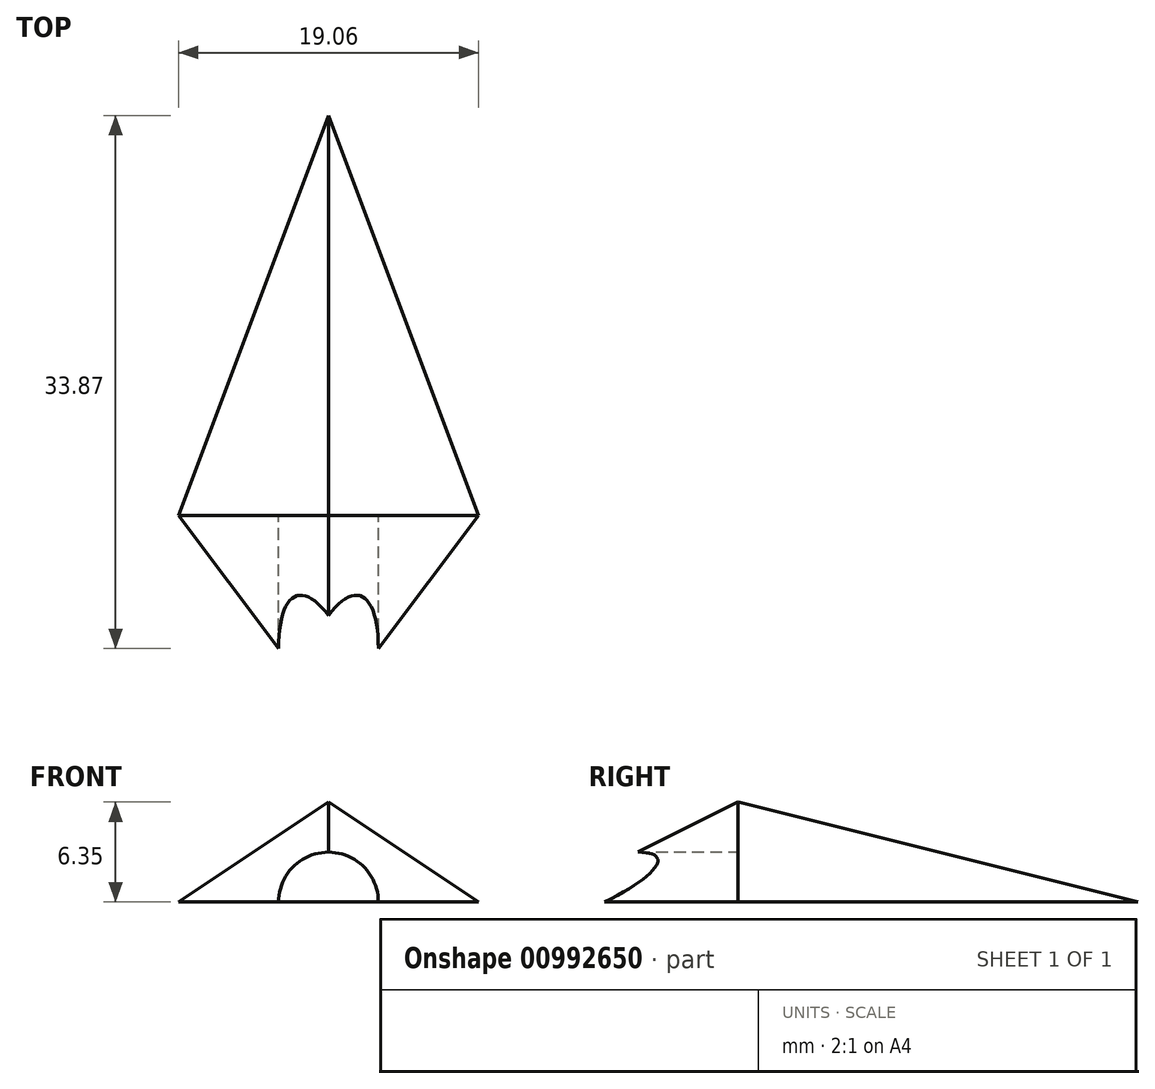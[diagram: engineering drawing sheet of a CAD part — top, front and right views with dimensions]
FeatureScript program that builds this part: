
annotation { "Feature Type Name" : "Feature", "Feature Type Description" : "" }
export const myFeature = defineFeature(function(context is Context, id is Id, definition is map)
    precondition{}
    {
        {
            var Q0;
            Q0=qCreatedBy(makeId("Top.planeOp"),FACE);
            var sketch = newSketch(context, id + "F0", { "sketchPlane" : qUnion([Q0])});
            skLineSegment(sketch, "E0", {"start": v(-9.53, 0) * mm, "end": v(9.53, 0) * mm});
            skLineSegment(sketch, "E1", {"start": v(0, -12.7) * mm, "end": v(0, 25.4) * mm});
            skLineSegment(sketch, "E2", {"start": v(-9.52, 0) * mm, "end": v(0, 25.4) * mm});
            skLineSegment(sketch, "E3", {"start": v(9.52, 0) * mm, "end": v(0, 25.4) * mm});
            skLineSegment(sketch, "E4", {"start": v(-9.53, 0) * mm, "end": v(0, -12.7) * mm});
            skLineSegment(sketch, "E5", {"start": v(9.53, 0) * mm, "end": v(0, -12.7) * mm});
            skSolve(sketch);
        }
        {
            var Q0;
            Q0=qCreatedBy(makeId("Right.planeOp"),FACE);
            var sketch = newSketch(context, id + "F1", { "sketchPlane" : qUnion([Q0])});
            skLineSegment(sketch, "E6", {"start": v(-12.7, 0) * mm, "end": v(25.4, 0) * mm});
            skLineSegment(sketch, "E7", {"start": v(0, 0) * mm, "end": v(0, 6.35) * mm});
            skLineSegment(sketch, "E8", {"start": v(25.4, 0) * mm, "end": v(0, 6.35) * mm});
            skLineSegment(sketch, "E9", {"start": v(-12.7, 0) * mm, "end": v(0, 6.35) * mm});
            skSolve(sketch);
        }
        {
            var Q0;
            Q0=qCreatedBy(makeId("Front.planeOp"),FACE);
            var sketch = newSketch(context, id + "F2", { "sketchPlane" : qUnion([Q0])});
            skLineSegment(sketch, "E10", {"start": v(-9.53, 0) * mm, "end": v(0, 6.35) * mm});
            skLineSegment(sketch, "E11", {"start": v(0, 6.35) * mm, "end": v(9.53, 0) * mm});
            skLineSegment(sketch, "E12", {"start": v(9.53, 0) * mm, "end": v(-9.53, 0) * mm});
            skSolve(sketch);
        }
        {
            var Q0;
            {var subQ2=sQuery(id+"F1.wireOp",EDGE,"E7");Q0=makeQuery(id+"F1.imprint","IMPRINT",FACE,{"disambiguationData":[TD([[makeQuery(id+"F1.imprint","IMPRINT",EDGE,{"derivedFrom":subQ2}),-1.0]])]});}
            var Q1;
            {var subQ0=sQuery(id+"F0.wireOp",EDGE,"E2");Q1=makeQuery(id+"F0.imprint","IMPRINT",FACE,{"disambiguationData":[TD([[makeQuery(id+"F0.imprint","IMPRINT",EDGE,{"derivedFrom":subQ0}),-1.0]])]});}
            var Q2;
            Q2=sQuery(id+"F2.wireOp",EDGE,"E10");
            loft(context, id + "F3", {"addGuides" : true, "sheetProfilesArray" : [{ "sheetProfileEntities" : qUnion([Q0]) }, { "sheetProfileEntities" : qUnion([Q1]) }], "guidesArray" : [{ "guideEntities" : qUnion([Q2]), "guideDerivativeType" : LoftGuideDerivativeType.DEFAULT, "guideDerivativeMagnitude" : 1 }]});
        }
        {
            var Q1;
            {var subQ2=sQuery(id+"F1.wireOp",EDGE,"E7");Q1=makeQuery(id+"F1.imprint","IMPRINT",FACE,{"disambiguationData":[TD([[makeQuery(id+"F1.imprint","IMPRINT",EDGE,{"derivedFrom":subQ2}),1.0]])]});}
            var Q2;
            {var subQ0=sQuery(id+"F0.wireOp",EDGE,"E4");Q2=makeQuery(id+"F0.imprint","IMPRINT",FACE,{"disambiguationData":[TD([[makeQuery(id+"F0.imprint","IMPRINT",EDGE,{"derivedFrom":subQ0}),1.0]])]});}
            var Q3;
            Q3=sQuery(id+"F2.wireOp",EDGE,"E10");
            loft(context, id + "F4", {"operationType" : NewBodyOperationType.ADD, "addGuides" : true, "sheetProfilesArray" : [{ "sheetProfileEntities" : qUnion([Q1]) }, { "sheetProfileEntities" : qUnion([Q2]) }], "guidesArray" : [{ "guideEntities" : qUnion([Q3]), "guideDerivativeType" : LoftGuideDerivativeType.DEFAULT, "guideDerivativeMagnitude" : 1 }]});
        }
        {
            var Q1;
            {var subQ2=sQuery(id+"F1.wireOp",EDGE,"E7");Q1=makeQuery(id+"F1.imprint","IMPRINT",FACE,{"disambiguationData":[TD([[makeQuery(id+"F1.imprint","IMPRINT",EDGE,{"derivedFrom":subQ2}),1.0]])]});}
            var Q2;
            {var subQ0=sQuery(id+"F0.wireOp",EDGE,"E5");Q2=makeQuery(id+"F0.imprint","IMPRINT",FACE,{"disambiguationData":[TD([[makeQuery(id+"F0.imprint","IMPRINT",EDGE,{"derivedFrom":subQ0}),-1.0]])]});}
            var Q3;
            Q3=sQuery(id+"F2.wireOp",EDGE,"E11");
            loft(context, id + "F5", {"operationType" : NewBodyOperationType.ADD, "addGuides" : true, "sheetProfilesArray" : [{ "sheetProfileEntities" : qUnion([Q1]) }, { "sheetProfileEntities" : qUnion([Q2]) }], "guidesArray" : [{ "guideEntities" : qUnion([Q3]), "guideDerivativeType" : LoftGuideDerivativeType.DEFAULT, "guideDerivativeMagnitude" : 1 }]});
        }
        {
            var Q1;
            {var subQ2=sQuery(id+"F1.wireOp",EDGE,"E7");Q1=makeQuery(id+"F1.imprint","IMPRINT",FACE,{"disambiguationData":[TD([[makeQuery(id+"F1.imprint","IMPRINT",EDGE,{"derivedFrom":subQ2}),-1.0]])]});}
            var Q2;
            {var subQ0=sQuery(id+"F0.wireOp",EDGE,"E3");Q2=makeQuery(id+"F0.imprint","IMPRINT",FACE,{"disambiguationData":[TD([[makeQuery(id+"F0.imprint","IMPRINT",EDGE,{"derivedFrom":subQ0}),1.0]])]});}
            var Q3;
            Q3=sQuery(id+"F2.wireOp",EDGE,"E11");
            loft(context, id + "F6", {"operationType" : NewBodyOperationType.ADD, "addGuides" : true, "sheetProfilesArray" : [{ "sheetProfileEntities" : qUnion([Q1]) }, { "sheetProfileEntities" : qUnion([Q2]) }], "guidesArray" : [{ "guideEntities" : qUnion([Q3]), "guideDerivativeType" : LoftGuideDerivativeType.DEFAULT, "guideDerivativeMagnitude" : 1 }]});
        }
        {
            var Q0;
            Q0=qCreatedBy(makeId("Front.planeOp"),FACE);
            var sketch = newSketch(context, id + "F7", { "sketchPlane" : qUnion([Q0])});
            skCircle(sketch, "E13", {"center": v(0, 0) * mm, "radius": 3.18 * mm});
            skSolve(sketch);
        }
        {
            var Q0;
            Q0=makeQuery(id+"F7.imprint","IMPRINT",FACE,{"disambiguationData":[TD([[makeQuery(id+"F7.imprint","IMPRINT",EDGE,{"derivedFrom":sQuery(id+"F7.wireOp",EDGE,"E13")}),1.0]])]});
            var Q1;
            Q1=sQuery(id+"F7.wireOp",EDGE,"E13");
            extrude(context, id + "F8", {"entities" : qUnion([Q0]), "operationType" : NewBodyOperationType.REMOVE, "surfaceEntities" : qUnion([Q1]), "depth" : 25.4 * mm, "offsetDistance" : 25.4 * mm});
        }
    });
